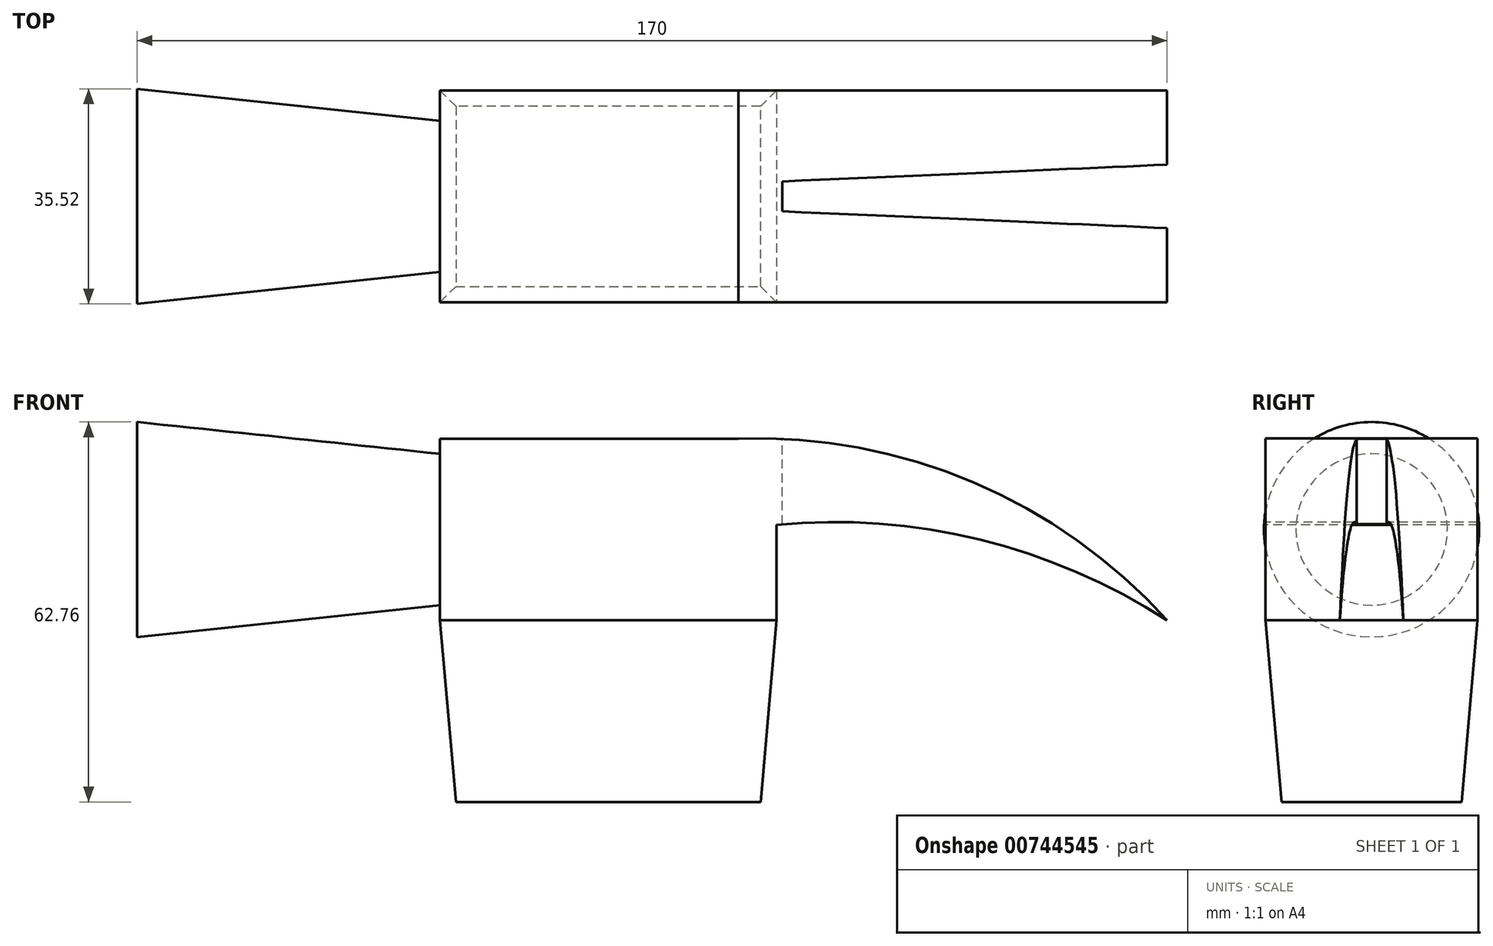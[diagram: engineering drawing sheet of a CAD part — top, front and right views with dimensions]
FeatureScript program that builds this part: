
annotation { "Feature Type Name" : "Feature", "Feature Type Description" : "" }
export const myFeature = defineFeature(function(context is Context, id is Id, definition is map)
    precondition{}
    {
        {
            var Q0;
            Q0=qCreatedBy(makeId("Front.planeOp"),FACE);
            var sketch = newSketch(context, id + "F0", { "sketchPlane" : qUnion([Q0])});
            skLineSegment(sketch, "E0.bottom", {"start": v(0, 0) * mm, "end": v(55.54, 0) * mm});
            skLineSegment(sketch, "E0.top", {"start": v(0, 30) * mm, "end": v(55.54, 30) * mm});
            skLineSegment(sketch, "E0.left", {"start": v(0, 0) * mm, "end": v(0, 30) * mm});
            skLineSegment(sketch, "E0.right", {"start": v(55.54, 0) * mm, "end": v(55.54, 30) * mm});
            skSolve(sketch);
        }
        {
            var Q0;
            Q0=qSketchRegion(id+"F0",true);
            extrude(context, id + "F1", {"entities" : qUnion([Q0]), "endBound" : BoundingType.SYMMETRIC, "depth" : 35 * mm, "offsetDistance" : 25 * mm});
        }
        {
            var Q0;
            Q0=makeQuery(id+"F1.opExtrude","SWEPT_FACE",FACE,{"disambiguationData":[OSD([sQuery(id+"F0.wireOp",EDGE,"E0.bottom")])]});
            extrude(context, id + "F2", {"entities" : qUnion([Q0]), "operationType" : NewBodyOperationType.ADD, "depth" : 30 * mm, "offsetDistance" : 25 * mm, "hasDraft" : true, "draftAngle" : 5 * degree, "draftPullDirection" : true});
        }
        {
            var Q0;
            Q0=makeQuery(id+"F1.opExtrude","SWEPT_FACE",FACE,{"disambiguationData":[OSD([sQuery(id+"F0.wireOp",EDGE,"E0.left")])]});
            var sketch = newSketch(context, id + "F3", { "sketchPlane" : qUnion([Q0])});
            skCircle(sketch, "E1", {"center": v(0, 15) * mm, "radius": 12.5 * mm});
            skSolve(sketch);
        }
        {
            var Q0;
            Q0 = qSketchRegion(id + "F3", true);
            extrude(context, id + "F4", {"entities" : qUnion([Q0]), "operationType" : NewBodyOperationType.ADD, "depth" : 50 * mm, "offsetDistance" : 25 * mm, "hasDraft" : true, "draftAngle" : 6 * degree});
        }
        {
            var Q0;
            Q0=makeQuery(id+"F1.opExtrude","CAP_FACE",FACE,{"disambiguationData":[OSD([sQuery(id+"F0.wireOp",EDGE,"E0.bottom"),sQuery(id+"F0.wireOp",EDGE,"E0.top"),sQuery(id+"F0.wireOp",EDGE,"E0.left"),sQuery(id+"F0.wireOp",EDGE,"E0.right")])],"isStart":false});
            var sketch = newSketch(context, id + "F5", { "sketchPlane" : qUnion([Q0])});
            skLineSegment(sketch, "E2", {"start": v(49.28, 30) * mm, "end": v(49.28, 15) * mm});
            skArc(sketch, "E3", {"start": v(120, 0) * mm, "mid": v(87.96, 22.83) * mm, "end": v(49.28, 30) * mm});
            skArc(sketch, "E4", {"start": v(120, 0) * mm, "mid": v(86.02, 14.03) * mm, "end": v(49.28, 15) * mm});
            skSolve(sketch);
        }
        {
            var Q0;
            Q0 = qSketchRegion(id + "F5", true);
            extrude(context, id + "F6", {"entities" : qUnion([Q0]), "operationType" : NewBodyOperationType.ADD, "oppositeDirection" : true, "depth" : 35 * mm, "offsetDistance" : 25 * mm});
        }
        {
            var Q0;
            Q0=makeQuery(id+"F1.opExtrude","SWEPT_FACE",FACE,{"disambiguationData":[OSD([sQuery(id+"F0.wireOp",EDGE,"E0.top")])]});
            var sketch = newSketch(context, id + "F7", { "sketchPlane" : qUnion([Q0])});
            skLineSegment(sketch, "E5", {"start": v(56.51, 2.47) * mm, "end": v(147.9, 6.46) * mm});
            skLineSegment(sketch, "E6", {"start": v(56.51, -2.47) * mm, "end": v(147.87, -6.46) * mm});
            skLineSegment(sketch, "E7", {"start": v(147.87, -6.46) * mm, "end": v(147.9, 6.46) * mm});
            skLineSegment(sketch, "E8", {"start": v(56.51, -2.47) * mm, "end": v(56.51, 2.47) * mm});
            skPoint(sketch, "E9.orphan", {"position": v(0, 0) * mm});
            skSolve(sketch);
        }
        {
            var Q0;
            Q0 = qSketchRegion(id + "F7", true);
            extrude(context, id + "F8", {"entities" : qUnion([Q0]), "operationType" : NewBodyOperationType.REMOVE, "oppositeDirection" : true, "depth" : 35 * mm, "offsetDistance" : 25 * mm});
        }
    });
